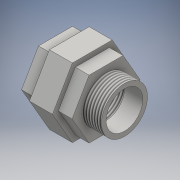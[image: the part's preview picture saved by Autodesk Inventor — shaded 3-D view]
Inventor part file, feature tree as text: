
AUTODESK INVENTOR PART (.ipt)
format: ipt  version: 2016 (Build 200138000, 138)  size: 138,752 bytes
history: native  units: mm
features: extrude x3, sketch x3, thread x2
ambient origin geometry x8: Origin, YZ Plane, XZ Plane, XY Plane, X Axis, Y Axis, Z Axis, Center Point
bodies: Solid1 (feature_tree)
feature tree (8):
  extrude  "Extrusion1"  Depth=64.0mm
  extrude  "Extrusion2"  Depth=50.0mm
  thread  "Thread1"  [1 undecoded]
  extrude  "Extrusion4"  Depth=10.0mm
  thread  "Thread2"  [1 undecoded]
  sketch  "Sketch1"  dims[d0=100.0mm d1=64.0mm]
  sketch  "Sketch3"  dims[d2=110.0mm d3=0.0mm d4=75.0mm d5=50.0mm d6=0.0mm]
  sketch  "Sketch4"  dims[d7=10.0mm d8=0.0mm d12=10.0mm d13=40.0mm d14=0.0mm d15=10.0mm d16=0.0mm]
note: 2 required parameter values undecoded (feature->parameter linkage not recoverable at this tier; creation-order binding heuristic only, values carry confidence <= 0.55)
